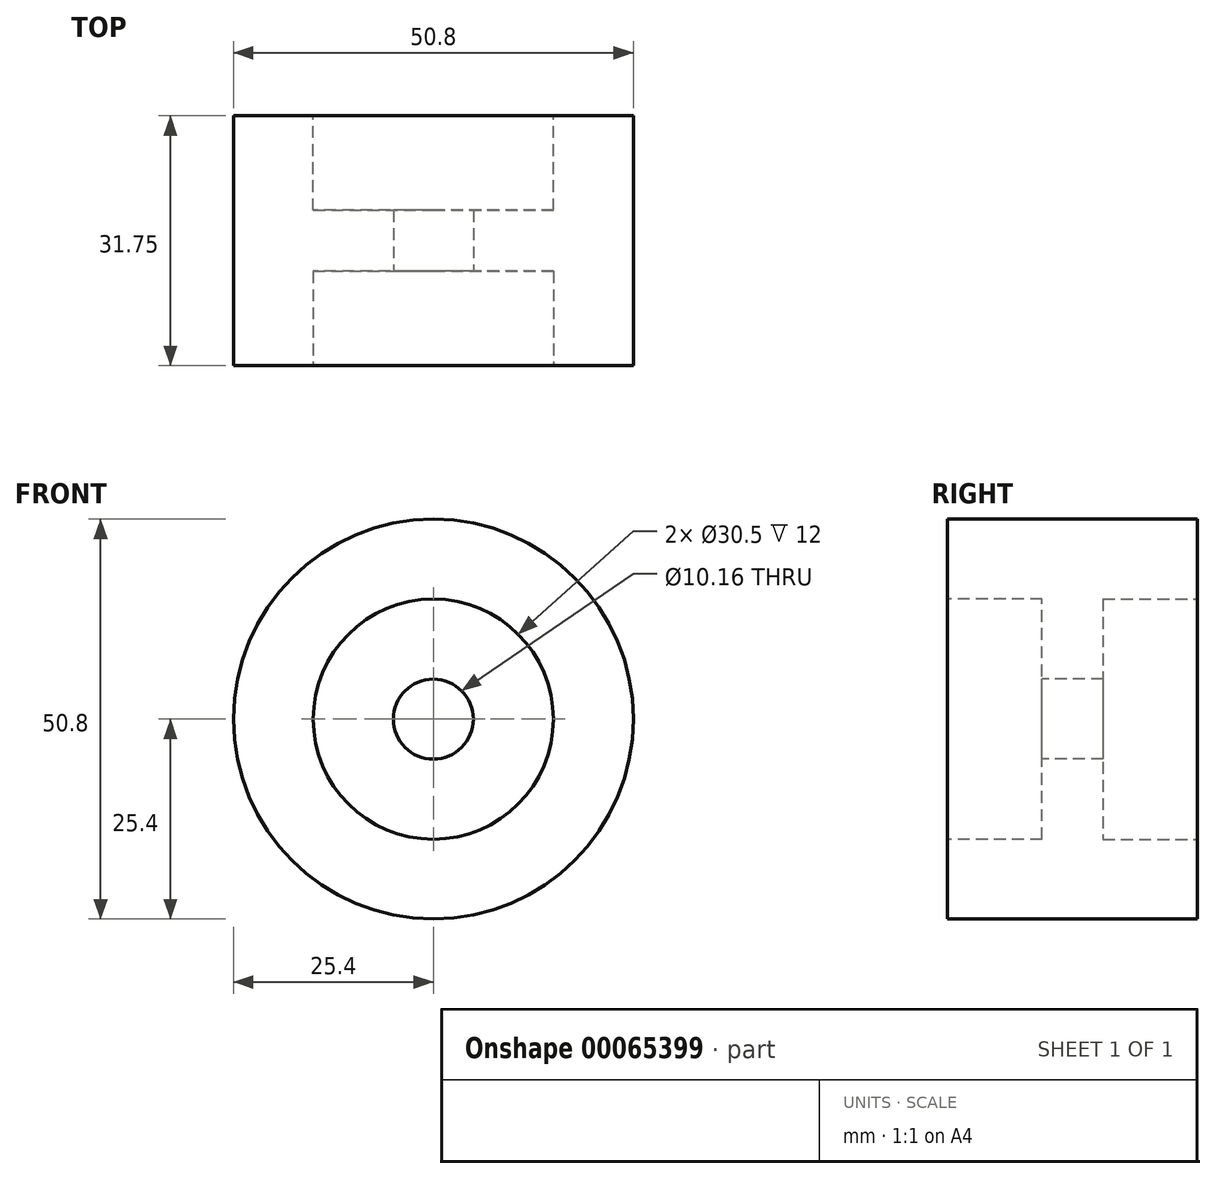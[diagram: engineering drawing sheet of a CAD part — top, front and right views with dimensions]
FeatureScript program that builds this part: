
annotation { "Feature Type Name" : "Feature", "Feature Type Description" : "" }
export const myFeature = defineFeature(function(context is Context, id is Id, definition is map)
    precondition{}
    {
        {
            var Q0;
            Q0=qCreatedBy(makeId("Front.planeOp"),FACE);
            var sketch = newSketch(context, id + "F0", { "sketchPlane" : qUnion([Q0])});
            skCircle(sketch, "E0", {"center": v(0, 0) * mm, "radius": 25.4 * mm});
            skSolve(sketch);
        }
        {
            var Q0;
            Q0 = qSketchRegion(id + "F0", true);
            extrude(context, id + "F1", {"entities" : qUnion([Q0]), "depth" : 31.75 * mm});
        }
        {
            var Q0;
            Q0=makeQuery(id+"F1.opExtrude","CAP_FACE",FACE,{"disambiguationData":[OSD([sQuery(id+"F0.wireOp",EDGE,"E0")])],"isStart":false});
            var sketch = newSketch(context, id + "F2", { "sketchPlane" : qUnion([Q0])});
            skCircle(sketch, "E1", {"center": v(0, 0) * mm, "radius": 5.08 * mm});
            skSolve(sketch);
        }
        {
            var Q0;
            Q0 = qSketchRegion(id + "F2", true);
            extrude(context, id + "F3", {"entities" : qUnion([Q0]), "operationType" : NewBodyOperationType.REMOVE, "endBound" : BoundingType.THROUGH_ALL, "oppositeDirection" : true, "depth" : 25.4 * mm});
        }
        {
            var Q0;
            Q0=makeQuery(id+"F1.opExtrude","CAP_FACE",FACE,{"disambiguationData":[OSD([sQuery(id+"F0.wireOp",EDGE,"E0")])],"isStart":false});
            var sketch = newSketch(context, id + "F4", { "sketchPlane" : qUnion([Q0])});
            skCircle(sketch, "E2", {"center": v(0, 0) * mm, "radius": 15.25 * mm});
            skSolve(sketch);
        }
        {
            var Q0;
            Q0 = qSketchRegion(id + "F4", true);
            extrude(context, id + "F5", {"entities" : qUnion([Q0]), "operationType" : NewBodyOperationType.REMOVE, "oppositeDirection" : true, "depth" : 12 * mm});
        }
        {
            var Q0;
            Q0=makeQuery(id+"F1.opExtrude","CAP_FACE",FACE,{"disambiguationData":[OSD([sQuery(id+"F0.wireOp",EDGE,"E0")])],"isStart":true});
            var sketch = newSketch(context, id + "F6", { "sketchPlane" : qUnion([Q0])});
            skCircle(sketch, "E3", {"center": v(0, 0) * mm, "radius": 15.25 * mm});
            skSolve(sketch);
        }
        {
            var Q0;
            Q0 = qSketchRegion(id + "F6", true);
            extrude(context, id + "F7", {"entities" : qUnion([Q0]), "operationType" : NewBodyOperationType.REMOVE, "oppositeDirection" : true, "depth" : 12 * mm});
        }
    });
